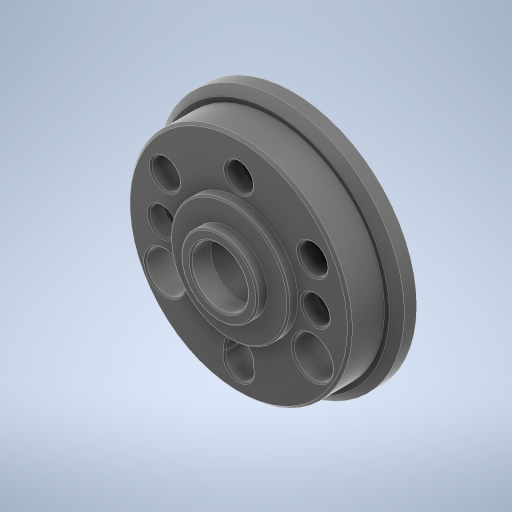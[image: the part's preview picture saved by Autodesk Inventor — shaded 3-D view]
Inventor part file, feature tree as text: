
AUTODESK INVENTOR PART (.ipt)
format: ipt  version: 2023 (Build 270158000, 158)  size: 433,152 bytes
history: native  units: mm
features: extrude x9, sketch x9, chamfer x3, fillet x1
ambient origin geometry x8: Origin, YZ Plane, XZ Plane, XY Plane, X Axis, Y Axis, Z Axis, Center Point
bodies: Solid1 (feature_tree)
feature tree (22):
  extrude  "Extrusion1"  Depth=40.0mm TaperAngle=360.0deg
  extrude  "Extrusion2"  Depth=50.0mm
  extrude  "Extrusion3"  Depth=4.75mm
  extrude  "Extrusion4"  Depth=60.0mm TaperAngle=360.0deg
  extrude  "Extrusion5"  Depth=11.0mm TaperAngle=360.0deg
  extrude  "Extrusion6"  Depth=5.5mm
  extrude  "Extrusion7"  Depth=3.2mm TaperAngle=0.0deg
  extrude  "Extrusion8"  Depth=3.1mm
  chamfer  "Chamfer1"  [1 undecoded]
  chamfer  "Chamfer2"  Distance=60.0mm Angle=360.0deg
  fillet  "Fillet1"  Radius=7.0mm
  extrude  "Extrusion9"  Depth=15.5mm
  chamfer  "Chamfer3"  Distance=2.0mm
  sketch  "Sketch1"  dims[d0=31.0mm d1=40.0mm d3=360.0deg]
  sketch  "Sketch2"  dims[d5=3.1mm d7=50.0mm]
  sketch  "Sketch3"  dims[d8=43.97mm d9=4.75mm]
  sketch  "Sketch4"  dims[d10=5.8mm d11=60.0mm d13=360.0deg]
  sketch  "Sketch5"  dims[d15=11.0mm d16=0.0mm d17=60.0mm d19=360.0deg]
  sketch  "Sketch6"  dims[d21=6.1mm d22=0.0mm d23=5.5mm]
  sketch  "Sketch7"  dims[d24=40.0mm d26=360.0deg d28=3.2mm d29=0.0mm]
  sketch  "Sketch8"  dims[d30=9.3mm d31=0.0mm d32=3.1mm d33=0.0mm d34=0.0mm]
  sketch  "Sketch9"  dims[d35=7.98mm d36=60.0mm d38=360.0deg d40=7.0mm d41=0.0mm d42=15.5mm d43=2.0mm d44=4.0mm d45=0.0mm d46=23.95mm d47=1.9mm d48=0.0mm d49=3.0mm d50=2.0mm d51=45.0deg d52=4.0mm d53=2.0mm d54=45.0deg d55=0.3mm d56=45.0mm d57=7.0mm d58=0.0mm d59=1.5mm d60=2.0mm d61=45.0deg]
note: 1 required parameter value undecoded (feature->parameter linkage not recoverable at this tier; creation-order binding heuristic only, values carry confidence <= 0.55)
